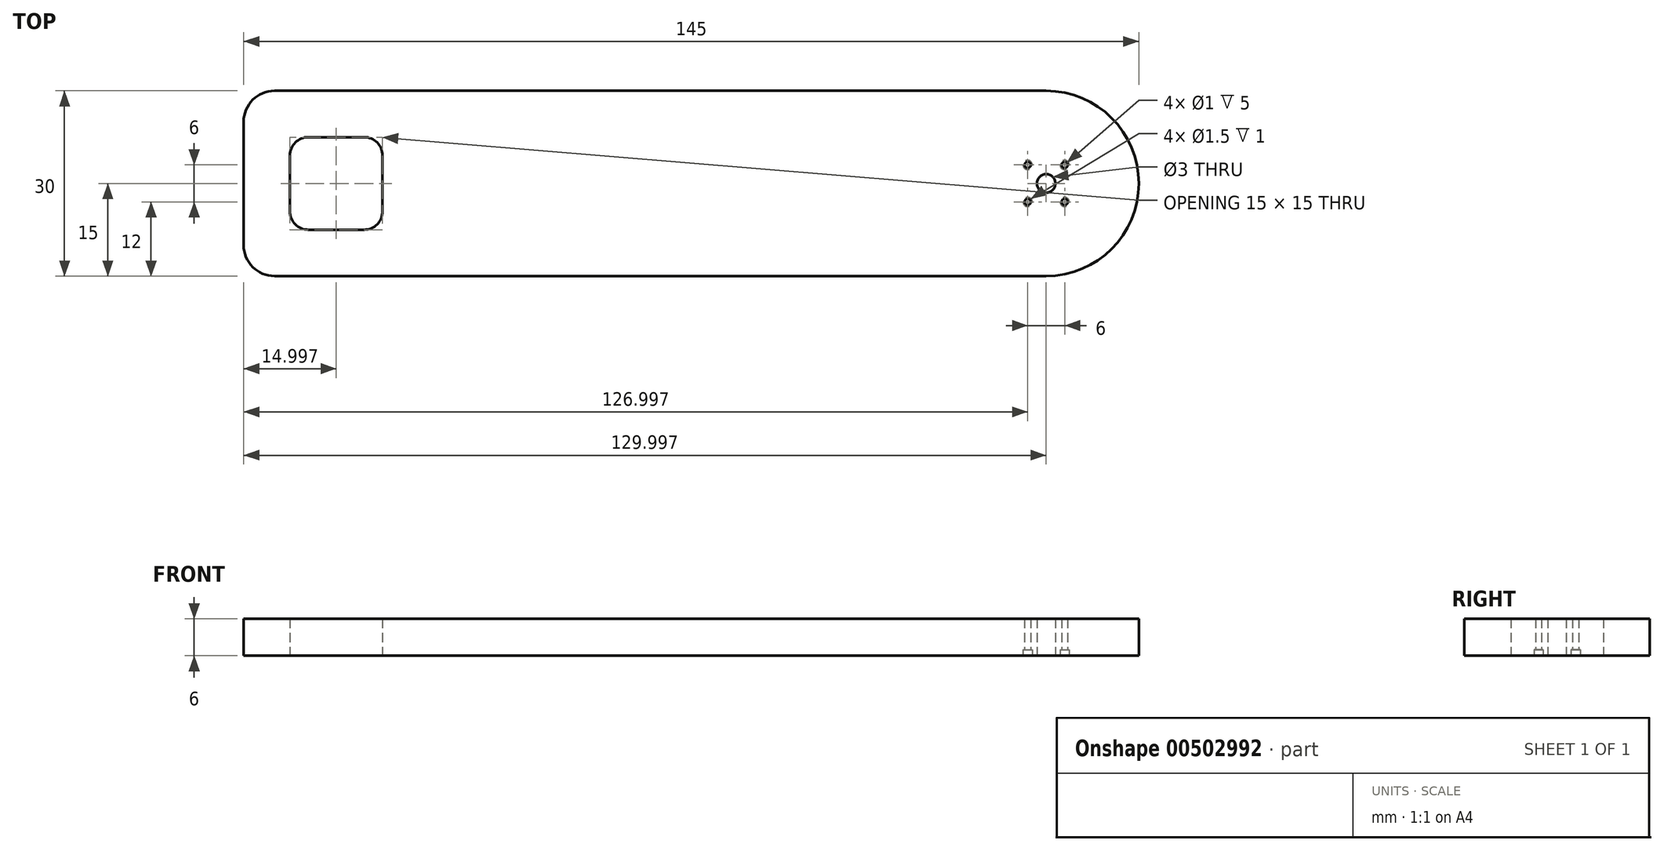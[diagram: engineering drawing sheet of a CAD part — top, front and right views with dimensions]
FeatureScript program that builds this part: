
annotation { "Feature Type Name" : "Feature", "Feature Type Description" : "" }
export const myFeature = defineFeature(function(context is Context, id is Id, definition is map)
    precondition{}
    {
        {
            var Q0;
            Q0=qCreatedBy(makeId("Top.planeOp"),FACE);
            var sketch = newSketch(context, id + "F0", { "sketchPlane" : qUnion([Q0])});
            skArc(sketch, "E0", {"start": v(52.72, 0) * mm, "mid": v(67.72, 15) * mm, "end": v(52.72, 30) * mm});
            skArc(sketch, "E1", {"start": v(52.72, 30) * mm, "mid": v(37.72, 15) * mm, "end": v(52.72, 0) * mm});
            skLineSegment(sketch, "E2", {"start": v(52.72, 0) * mm, "end": v(34.72, 0) * mm});
            skLineSegment(sketch, "E3", {"start": v(35.33, 30) * mm, "end": v(52.72, 30) * mm});
            skLineSegment(sketch, "E4.bottom", {"start": v(-47.28, 30) * mm, "end": v(-72.28, 30) * mm});
            skLineSegment(sketch, "E4.right", {"start": v(-77.28, 25) * mm, "end": v(-77.28, 5) * mm});
            skLineSegment(sketch, "E5", {"start": v(-72.28, 0) * mm, "end": v(16.73, 0) * mm});
            skArc(sketch, "E6.filletArc", {"start": v(-77.28, 5) * mm, "mid": v(-75.82, 1.46) * mm, "end": v(-72.28, 0) * mm});
            skArc(sketch, "E7.filletArc", {"start": v(-72.28, 30) * mm, "mid": v(-75.82, 28.54) * mm, "end": v(-77.28, 25) * mm});
            skLineSegment(sketch, "E8.bottom", {"start": v(-66.78, 22.5) * mm, "end": v(-57.78, 22.5) * mm});
            skLineSegment(sketch, "E8.top", {"start": v(-66.78, 7.5) * mm, "end": v(-57.78, 7.5) * mm});
            skLineSegment(sketch, "E8.left", {"start": v(-69.78, 19.5) * mm, "end": v(-69.78, 10.5) * mm});
            skLineSegment(sketch, "E8.right", {"start": v(-54.78, 19.5) * mm, "end": v(-54.78, 10.5) * mm});
            skArc(sketch, "E9.filletArc", {"start": v(-66.78, 22.5) * mm, "mid": v(-68.9, 21.62) * mm, "end": v(-69.78, 19.5) * mm});
            skArc(sketch, "E10.filletArc", {"start": v(-54.78, 19.5) * mm, "mid": v(-55.66, 21.62) * mm, "end": v(-57.78, 22.5) * mm});
            skArc(sketch, "E11.filletArc", {"start": v(-57.78, 7.5) * mm, "mid": v(-55.66, 8.38) * mm, "end": v(-54.78, 10.5) * mm});
            skArc(sketch, "E12.filletArc", {"start": v(-69.78, 10.5) * mm, "mid": v(-68.9, 8.38) * mm, "end": v(-66.78, 7.5) * mm});
            skLineSegment(sketch, "E13", {"start": v(16.73, 0) * mm, "end": v(34.72, 0) * mm});
            skLineSegment(sketch, "E14", {"start": v(-47.28, 30) * mm, "end": v(35.33, 30) * mm});
            skLineSegment(sketch, "E15", {"start": v(52.72, 30) * mm, "end": v(52.72, 0) * mm});
            skPoint(sketch, "E16", {"position": v(49.72, 18) * mm});
            skPoint(sketch, "E17", {"position": v(49.72, 12) * mm});
            skPoint(sketch, "E18", {"position": v(55.72, 12) * mm});
            skPoint(sketch, "E19", {"position": v(55.72, 18) * mm});
            skSolve(sketch);
        }
        {
            var Q0;
            Q0 = qSketchRegion(id + "F0", true);
            extrude(context, id + "F1", {"entities" : qUnion([Q0]), "depth" : 6 * mm});
        }
        {
            var Q0;
            Q0=sQuery(id+"F0.wireOp",VERTEX,"E1.center");
            var Q1;
            Q1=makeQuery(id+"F1.opExtrude","SWEPT_BODY",BODY,{"disambiguationData":[OSD([sQuery(id+"F0.wireOp",EDGE,"E0"),sQuery(id+"F0.wireOp",EDGE,"E2"),sQuery(id+"F0.wireOp",EDGE,"E3"),sQuery(id+"F0.wireOp",EDGE,"E4.bottom"),sQuery(id+"F0.wireOp",EDGE,"E4.right"),sQuery(id+"F0.wireOp",EDGE,"E5"),sQuery(id+"F0.wireOp",EDGE,"E6.filletArc"),sQuery(id+"F0.wireOp",EDGE,"E7.filletArc"),sQuery(id+"F0.wireOp",EDGE,"E8.bottom"),sQuery(id+"F0.wireOp",EDGE,"E8.top"),sQuery(id+"F0.wireOp",EDGE,"E8.left"),sQuery(id+"F0.wireOp",EDGE,"E8.right"),sQuery(id+"F0.wireOp",EDGE,"E9.filletArc"),sQuery(id+"F0.wireOp",EDGE,"E10.filletArc"),sQuery(id+"F0.wireOp",EDGE,"E11.filletArc"),sQuery(id+"F0.wireOp",EDGE,"E12.filletArc"),sQuery(id+"F0.wireOp",EDGE,"E13"),sQuery(id+"F0.wireOp",EDGE,"E14")])]});
            hole(context, id + "F2", {"style" : HoleStyle.SIMPLE, "endStyle" : HoleEndStyle.THROUGH, "oppositeDirection" : true, "holeDiameter" : 3 * mm, "isTappedThrough" : true, "tappedDepth" : 12 * mm, "tapClearance" : 3, "locations" : qUnion([Q0]), "scope" : qUnion([Q1])});
        }
        {
            var Q0;
            Q0=sQuery(id+"F0.wireOp",VERTEX,"E19");
            var Q1;
            Q1=sQuery(id+"F0.wireOp",VERTEX,"E18");
            var Q2;
            Q2=sQuery(id+"F0.wireOp",VERTEX,"E17");
            var Q3;
            Q3=sQuery(id+"F0.wireOp",VERTEX,"E16");
            var Q4;
            Q4=makeQuery(id+"F1.opExtrude","SWEPT_BODY",BODY,{"disambiguationData":[OSD([sQuery(id+"F0.wireOp",EDGE,"E0"),sQuery(id+"F0.wireOp",EDGE,"E2"),sQuery(id+"F0.wireOp",EDGE,"E3"),sQuery(id+"F0.wireOp",EDGE,"E4.bottom"),sQuery(id+"F0.wireOp",EDGE,"E4.right"),sQuery(id+"F0.wireOp",EDGE,"E5"),sQuery(id+"F0.wireOp",EDGE,"E6.filletArc"),sQuery(id+"F0.wireOp",EDGE,"E7.filletArc"),sQuery(id+"F0.wireOp",EDGE,"E8.bottom"),sQuery(id+"F0.wireOp",EDGE,"E8.top"),sQuery(id+"F0.wireOp",EDGE,"E8.left"),sQuery(id+"F0.wireOp",EDGE,"E8.right"),sQuery(id+"F0.wireOp",EDGE,"E9.filletArc"),sQuery(id+"F0.wireOp",EDGE,"E10.filletArc"),sQuery(id+"F0.wireOp",EDGE,"E11.filletArc"),sQuery(id+"F0.wireOp",EDGE,"E12.filletArc"),sQuery(id+"F0.wireOp",EDGE,"E13"),sQuery(id+"F0.wireOp",EDGE,"E14")])]});
            hole(context, id + "F3", {"style" : HoleStyle.C_BORE, "endStyle" : HoleEndStyle.THROUGH, "oppositeDirection" : true, "holeDiameter" : 1 * mm, "cBoreDiameter" : 1.5 * mm, "cBoreDepth" : 1 * mm, "isTappedThrough" : true, "tappedDepth" : 12 * mm, "tapClearance" : 3, "locations" : qUnion([Q0, Q1, Q2, Q3]), "scope" : qUnion([Q4])});
        }
    });
